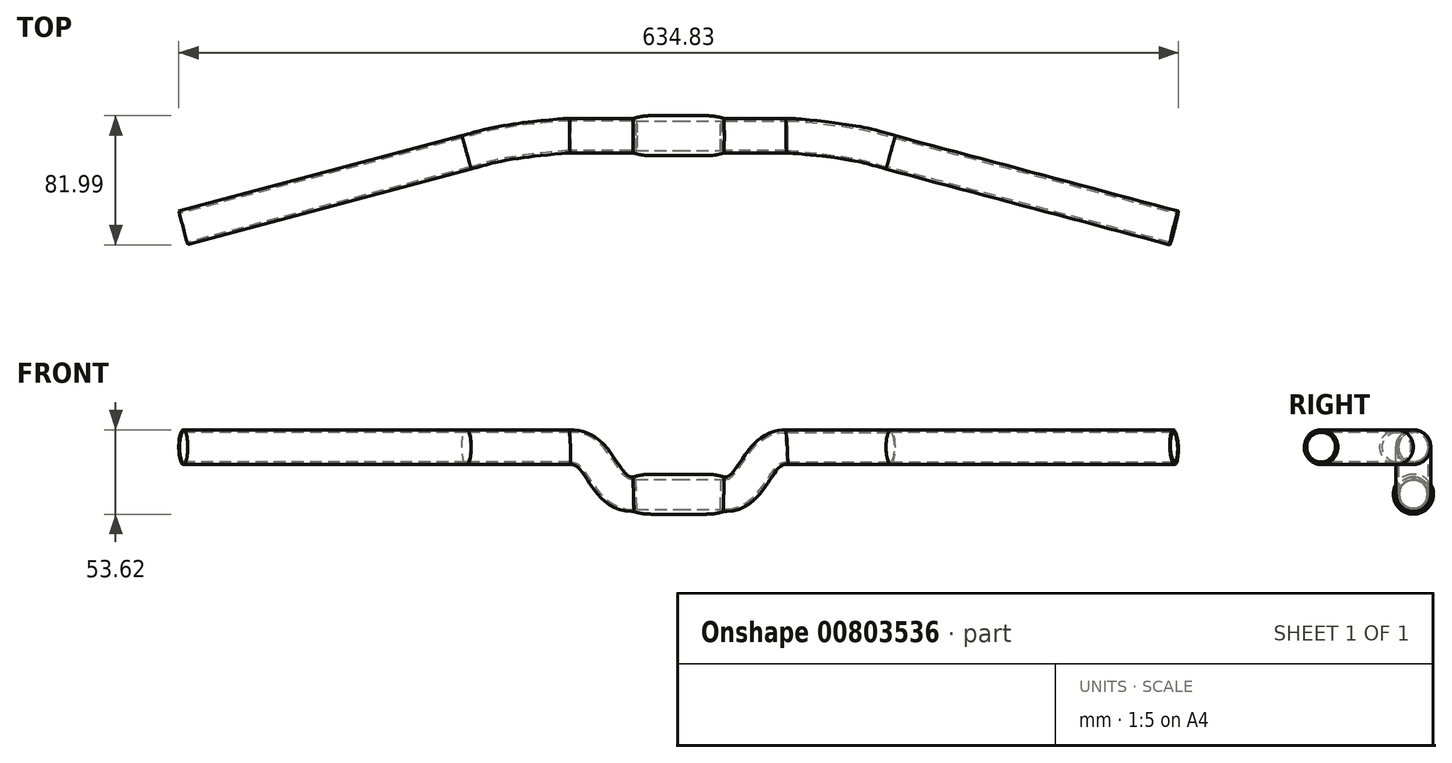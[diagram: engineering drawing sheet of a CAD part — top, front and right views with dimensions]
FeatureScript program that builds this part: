
annotation { "Feature Type Name" : "Feature", "Feature Type Description" : "" }
export const myFeature = defineFeature(function(context is Context, id is Id, definition is map)
    precondition{}
    {
        {
            var Q0;
            Q0=qCreatedBy(makeId("Top.planeOp"),FACE);
            var sketch = newSketch(context, id + "F0", { "sketchPlane" : qUnion([Q0])});
            skLineSegment(sketch, "E0", {"start": v(0, 0) * mm, "end": v(-317.5, 0) * mm, "construction": true});
            skPoint(sketch, "E1", {"position": v(-137.5, 0) * mm});
            skPoint(sketch, "E2", {"position": v(-32.8, 0) * mm});
            skPoint(sketch, "E3", {"position": v(-317.5, -48) * mm});
            skPoint(sketch, "E4", {"position": v(-94.59, 0) * mm});
            skLineSegment(sketch, "E5", {"start": v(-317.5, -48) * mm, "end": v(-137.5, 0) * mm});
            skLineSegment(sketch, "E6", {"start": v(-317.5, -48) * mm, "end": v(-311.83, -69.26) * mm});
            skLineSegment(sketch, "E7", {"start": v(-311.83, -69.26) * mm, "end": v(-131.83, -21.26) * mm});
            skLineSegment(sketch, "E8", {"start": v(-314.67, -58.63) * mm, "end": v(-134.67, -10.63) * mm});
            skFitSpline(sketch, "E9", {"points": [v(-134.67, -10.63) * mm, v(-110.33, -4.58) * mm, v(-68.56, 0) * mm], "startDerivative": vector(65.16, 18.57) * mm, "endDerivative": vector(34.07, 0) * mm});
            skArc(sketch, "E10.0.startCap", {"start": v(-131.65, -21.2) * mm, "mid": v(-145.24, -13.64) * mm, "end": v(-137.68, -0.05) * mm, "construction": true});
            skFitSpline(sketch, "E10.0.left", {"points": [v(-137.68, -0.05) * mm, v(-136.35, 0.33) * mm, v(-133.87, 1.05) * mm, v(-130.47, 2.04) * mm, v(-127.2, 2.97) * mm, v(-123.86, 3.85) * mm, v(-120.32, 4.7) * mm, v(-117.1, 5.37) * mm, v(-114.3, 5.9) * mm, v(-112.07, 6.28) * mm, v(-109.68, 6.67) * mm, v(-106.34, 7.19) * mm, v(-101.9, 7.81) * mm, v(-96.35, 8.53) * mm, v(-90.75, 9.2) * mm, v(-85.3, 9.78) * mm, v(-80.2, 10.28) * mm, v(-76.37, 10.6) * mm, v(-73.64, 10.8) * mm, v(-71.78, 10.9) * mm, v(-70.1, 10.98) * mm, v(-69.07, 11) * mm, v(-68.56, 11) * mm]});
            skFitSpline(sketch, "E10.0.right", {"points": [v(-131.65, -21.2) * mm, v(-128.88, -20.42) * mm, v(-125.36, -19.38) * mm, v(-121.34, -18.24) * mm, v(-118.47, -17.48) * mm, v(-115.53, -16.78) * mm, v(-112.82, -16.21) * mm, v(-110.4, -15.76) * mm, v(-107.76, -15.3) * mm, v(-104, -14.7) * mm, v(-98.96, -14) * mm, v(-93.65, -13.3) * mm, v(-88.27, -12.67) * mm, v(-83.04, -12.1) * mm, v(-78.18, -11.63) * mm, v(-74.62, -11.33) * mm, v(-72.2, -11.15) * mm, v(-70.63, -11.06) * mm, v(-69.36, -11) * mm, v(-68.77, -11) * mm, v(-68.56, -11) * mm]});
            skLineSegment(sketch, "E11", {"start": v(-68.56, 0) * mm, "end": v(-32.8, 0) * mm});
            skFitSpline(sketch, "E12.MirrorCS", {"points": [v(134.67, -10.63) * mm, v(110.33, -4.58) * mm, v(68.56, 0) * mm], "startDerivative": vector(-65.16, 18.57) * mm, "endDerivative": vector(-34.07, 0) * mm});
            skLineSegment(sketch, "E13.MirrorCS", {"start": v(314.67, -58.63) * mm, "end": v(134.67, -10.63) * mm});
            skSolve(sketch);
        }
        {
            var Q0;
            Q0=qCreatedBy(makeId("Right.planeOp"),FACE);
            cPlane(context, id + "F1", {"entities" : qUnion([Q0]), "cplaneType" : CPlaneType.OFFSET, "offset" : 68.5 * mm, "oppositeDirection" : true, "width" : 150 * mm, "height" : 150 * mm});
        }
        {
            var Q0;
            Q0=qCreatedBy(id+"F1.planeOp",FACE);
            var sketch = newSketch(context, id + "F2", { "sketchPlane" : qUnion([Q0])});
            skCircle(sketch, "E14", {"center": v(0, 0) * mm, "radius": 11 * mm});
            skCircle(sketch, "E15", {"center": v(0, 0) * mm, "radius": 9.45 * mm});
            skSolve(sketch);
        }
        {
            var Q0;
            Q0=makeQuery(id+"F2.imprint","IMPRINT",FACE,{"disambiguationData":[TD([[makeQuery(id+"F2.imprint","IMPRINT",EDGE,{"derivedFrom":sQuery(id+"F2.wireOp",EDGE,"E14")}),1.0]])]});
            var Q1;
            Q1=sQuery(id+"F0.wireOp",EDGE,"E9");
            var Q2;
            Q2=sQuery(id+"F0.wireOp",EDGE,"E8");
            sweep(context, id + "F3", {"profiles" : qUnion([Q0]), "path" : qUnion([Q1, Q2])});
        }
        {
            var Q0;
            Q0=qCreatedBy(makeId("Front.planeOp"),FACE);
            var sketch = newSketch(context, id + "F4", { "sketchPlane" : qUnion([Q0])});
            skLineSegment(sketch, "E16", {"start": v(0, 0) * mm, "end": v(0, -52) * mm});
            skPoint(sketch, "E17", {"position": v(0, -30) * mm});
            skLineSegment(sketch, "E18", {"start": v(0, -30) * mm, "end": v(-30, -30) * mm});
            skPoint(sketch, "E19.0.internal.orphan", {"position": v(-69, 0) * mm});
            skFitSpline(sketch, "E20", {"points": [v(-69, 0) * mm, v(-58.9, -2.84) * mm, v(-50.06, -12.92) * mm, v(-40.1, -25.77) * mm, v(-30, -30) * mm], "startDerivative": vector(46.65, -0.49) * mm, "endDerivative": vector(45.78, -0.22) * mm});
            skLineSegment(sketch, "E21.MirrorCS", {"start": v(0, -30) * mm, "end": v(30, -30) * mm});
            skFitSpline(sketch, "E22.MirrorCS", {"points": [v(69, 0) * mm, v(58.9, -2.84) * mm, v(50.06, -12.92) * mm, v(40.1, -25.77) * mm, v(30, -30) * mm], "startDerivative": vector(-46.65, -0.49) * mm, "endDerivative": vector(-45.78, -0.22) * mm});
            skSolve(sketch);
        }
        {
            var Q0;
            Q0=makeQuery(id+"F3.opSweep","CAP_FACE",FACE,{"disambiguationData":[OSD([sQuery(id+"F0.wireOp",VERTEX,"E9.end"),sQuery(id+"F2.wireOp",EDGE,"E14"),sQuery(id+"F2.wireOp",EDGE,"E15")])],"isStart":true});
            var Q1;
            Q1=sQuery(id+"F4.wireOp",EDGE,"E20");
            var Q2;
            Q2=sQuery(id+"F4.wireOp",EDGE,"E18");
            sweep(context, id + "F5", {"operationType" : NewBodyOperationType.ADD, "profiles" : qUnion([Q0]), "path" : qUnion([Q1, Q2])});
        }
        {
            var Q0;
            Q0=makeQuery(id+"F5.opSweep","CAP_FACE",FACE,{"disambiguationData":[OSD([sQuery(id+"F0.wireOp",VERTEX,"E9.end"),sQuery(id+"F2.wireOp",EDGE,"E14"),sQuery(id+"F2.wireOp",EDGE,"E15"),sQuery(id+"F4.wireOp",VERTEX,"E18.start")])],"isStart":false});
            var Q1;
            Q1=sQuery(id+"F4.wireOp",EDGE,"E21.MirrorCS");
            var Q2;
            Q2=sQuery(id+"F4.wireOp",EDGE,"E22.MirrorCS");
            sweep(context, id + "F6", {"operationType" : NewBodyOperationType.ADD, "profiles" : qUnion([Q0]), "path" : qUnion([Q1, Q2])});
        }
        {
            var Q0;
            Q0=makeQuery(id+"F6.opSweep","CAP_FACE",FACE,{"disambiguationData":[OSD([sQuery(id+"F0.wireOp",VERTEX,"E9.end"),sQuery(id+"F2.wireOp",EDGE,"E14"),sQuery(id+"F2.wireOp",EDGE,"E15"),sQuery(id+"F4.wireOp",VERTEX,"E18.start"),sQuery(id+"F4.wireOp",VERTEX,"E22.MirrorCS.start")])],"isStart":false});
            var Q1;
            Q1=sQuery(id+"F0.wireOp",EDGE,"E12.MirrorCS");
            var Q2;
            Q2=sQuery(id+"F0.wireOp",EDGE,"E13.MirrorCS");
            sweep(context, id + "F7", {"operationType" : NewBodyOperationType.ADD, "profiles" : qUnion([Q0]), "path" : qUnion([Q1, Q2])});
        }
        {
            var Q0;
            Q0=qCreatedBy(makeId("Front.planeOp"),FACE);
            var sketch = newSketch(context, id + "F8", { "sketchPlane" : qUnion([Q0])});
            skLineSegment(sketch, "E23", {"start": v(0, -42.61) * mm, "end": v(0, -19.21) * mm});
            skLineSegment(sketch, "E24", {"start": v(0, -17.21) * mm, "end": v(15.78, -17.21) * mm});
            skLineSegment(sketch, "E25", {"start": v(15.78, -19.21) * mm, "end": v(15.78, -42.61) * mm});
            skLineSegment(sketch, "E26", {"start": v(15.78, -42.61) * mm, "end": v(0, -42.61) * mm});
            skLineSegment(sketch, "E27.MirrorCS", {"start": v(0, -17.21) * mm, "end": v(-15.78, -17.21) * mm});
            skLineSegment(sketch, "E28.MirrorCS", {"start": v(-15.78, -19.21) * mm, "end": v(-15.78, -42.61) * mm});
            skLineSegment(sketch, "E29.MirrorCS", {"start": v(-15.78, -42.61) * mm, "end": v(0, -42.61) * mm});
            skFitSpline(sketch, "E30", {"points": [v(15.78, -17.21) * mm, v(22.33, -17.5) * mm, v(29.37, -19.1) * mm], "startDerivative": vector(13.34, 0.01) * mm, "endDerivative": vector(13.84, -3.76) * mm});
            skLineSegment(sketch, "E31", {"start": v(15.78, -29.91) * mm, "end": v(22.66, -29.91) * mm});
            skFitSpline(sketch, "E32.MirrorCS", {"points": [v(15.78, -42.61) * mm, v(22.33, -42.32) * mm, v(29.37, -40.73) * mm], "startDerivative": vector(13.34, -0.01) * mm, "endDerivative": vector(13.84, 3.76) * mm});
            skFitSpline(sketch, "E33.MirrorCS", {"points": [v(-15.78, -17.21) * mm, v(-22.33, -17.5) * mm, v(-29.37, -19.1) * mm], "startDerivative": vector(-13.34, 0.01) * mm, "endDerivative": vector(-13.84, -3.76) * mm});
            skFitSpline(sketch, "E34.MirrorCS", {"points": [v(-15.78, -42.61) * mm, v(-22.33, -42.32) * mm, v(-29.37, -40.73) * mm], "startDerivative": vector(-13.34, -0.01) * mm, "endDerivative": vector(-13.84, 3.76) * mm});
            skFitSpline(sketch, "E35.0", {"points": [v(-15.78, -19.21) * mm, v(-16.33, -19.21) * mm, v(-17.43, -19.21) * mm, v(-19.05, -19.24) * mm, v(-20.38, -19.31) * mm, v(-21.43, -19.4) * mm, v(-22.2, -19.5) * mm, v(-23, -19.63) * mm, v(-24.07, -19.83) * mm, v(-25.44, -20.13) * mm, v(-27.12, -20.56) * mm, v(-28.27, -20.87) * mm, v(-28.84, -21.03) * mm]});
            skFitSpline(sketch, "E36.0", {"points": [v(-15.78, -40.61) * mm, v(-16.33, -40.61) * mm, v(-17.43, -40.61) * mm, v(-19.05, -40.59) * mm, v(-20.38, -40.52) * mm, v(-21.43, -40.42) * mm, v(-22.2, -40.32) * mm, v(-23, -40.2) * mm, v(-24.07, -40) * mm, v(-25.44, -39.7) * mm, v(-27.12, -39.26) * mm, v(-28.27, -38.95) * mm, v(-28.84, -38.8) * mm]});
            skFitSpline(sketch, "E37.0", {"points": [v(15.78, -19.21) * mm, v(16.33, -19.21) * mm, v(17.43, -19.21) * mm, v(19.05, -19.24) * mm, v(20.38, -19.31) * mm, v(21.43, -19.4) * mm, v(22.2, -19.5) * mm, v(23, -19.63) * mm, v(24.07, -19.83) * mm, v(25.44, -20.13) * mm, v(27.12, -20.56) * mm, v(28.27, -20.87) * mm, v(28.84, -21.03) * mm]});
            skFitSpline(sketch, "E38.0", {"points": [v(15.78, -40.61) * mm, v(16.33, -40.61) * mm, v(17.43, -40.61) * mm, v(19.05, -40.59) * mm, v(20.38, -40.52) * mm, v(21.43, -40.42) * mm, v(22.2, -40.32) * mm, v(23, -40.2) * mm, v(24.07, -40) * mm, v(25.44, -39.7) * mm, v(27.12, -39.26) * mm, v(28.27, -38.95) * mm, v(28.84, -38.8) * mm]});
            skLineSegment(sketch, "E39", {"start": v(-29.37, -19.1) * mm, "end": v(-28.84, -21.03) * mm});
            skLineSegment(sketch, "E40", {"start": v(-28.84, -38.8) * mm, "end": v(-29.37, -40.73) * mm});
            skLineSegment(sketch, "E41", {"start": v(29.37, -19.1) * mm, "end": v(28.84, -21.03) * mm});
            skLineSegment(sketch, "E42", {"start": v(-15.78, -19.21) * mm, "end": v(15.78, -19.21) * mm});
            skSolve(sketch);
        }
        {
            var Q0;
            Q0=makeQuery(id+"F8.imprint","IMPRINT",FACE,{"disambiguationData":[TD([[makeQuery(id+"F8.imprint","IMPRINT",EDGE,{"derivedFrom":sQuery(id+"F8.wireOp",EDGE,"E24")}),-1.0]])]});
            var Q1;
            Q1=sQuery(id+"F8.wireOp",EDGE,"E31");
            revolve(context, id + "F9", {"operationType" : NewBodyOperationType.ADD, "surfaceOperationType" : NewSurfaceOperationType.NEW, "entities" : qUnion([Q0]), "axis" : qUnion([Q1]), "revolveType" : RevolveType.FULL});
        }
    });
